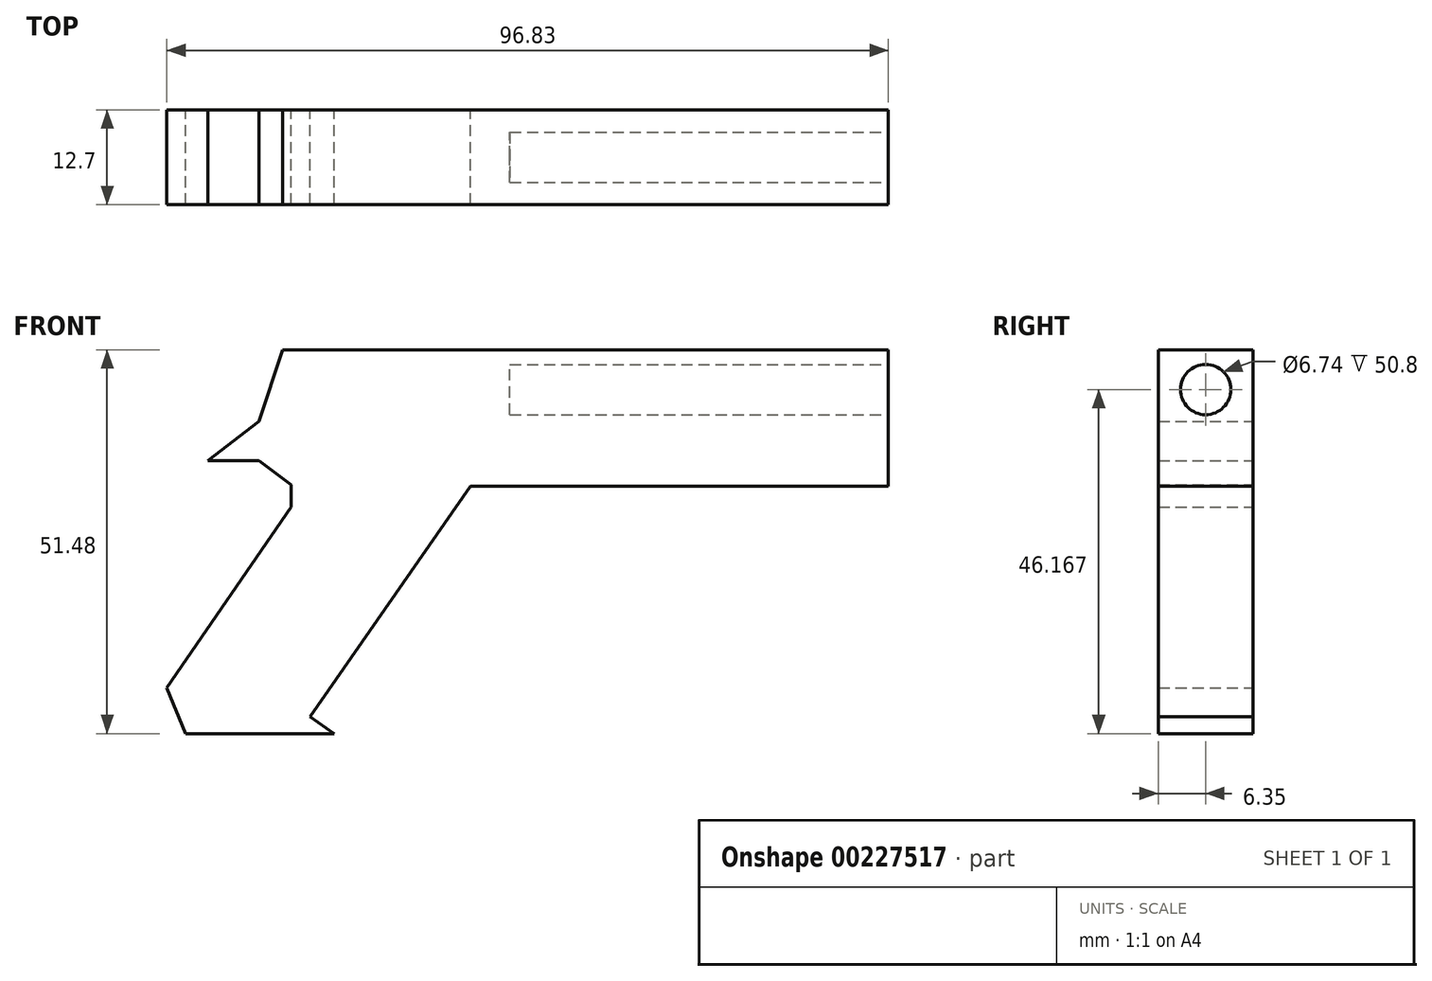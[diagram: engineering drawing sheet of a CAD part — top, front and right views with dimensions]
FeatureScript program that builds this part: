
annotation { "Feature Type Name" : "Feature", "Feature Type Description" : "" }
export const myFeature = defineFeature(function(context is Context, id is Id, definition is map)
    precondition{}
    {
        {
            var Q0;
            Q0=qCreatedBy(makeId("Front.planeOp"),FACE);
            var sketch = newSketch(context, id + "F0", { "sketchPlane" : qUnion([Q0])});
            skLineSegment(sketch, "E0", {"start": v(-32.16, 42.92) * mm, "end": v(49.1, 42.92) * mm});
            skLineSegment(sketch, "E1", {"start": v(49.1, 42.92) * mm, "end": v(49.1, 24.6) * mm});
            skLineSegment(sketch, "E2", {"start": v(49.1, 24.6) * mm, "end": v(-6.98, 24.6) * mm});
            skLineSegment(sketch, "E3", {"start": v(-6.98, 24.6) * mm, "end": v(-28.5, -6.3) * mm});
            skLineSegment(sketch, "E4", {"start": v(-28.5, -6.3) * mm, "end": v(-25.26, -8.56) * mm});
            skLineSegment(sketch, "E5", {"start": v(-25.26, -8.56) * mm, "end": v(-45.21, -8.56) * mm});
            skLineSegment(sketch, "E6", {"start": v(-45.21, -8.56) * mm, "end": v(-47.73, -2.4) * mm});
            skLineSegment(sketch, "E7", {"start": v(-47.73, -2.4) * mm, "end": v(-31.02, 21.86) * mm});
            skLineSegment(sketch, "E8", {"start": v(-31.02, 21.86) * mm, "end": v(-31.02, 24.84) * mm});
            skLineSegment(sketch, "E9", {"start": v(-31.02, 24.84) * mm, "end": v(-35.37, 28.04) * mm});
            skLineSegment(sketch, "E10", {"start": v(-35.37, 28.04) * mm, "end": v(-42.24, 28.04) * mm});
            skLineSegment(sketch, "E11", {"start": v(-42.24, 28.04) * mm, "end": v(-35.37, 33.3) * mm});
            skLineSegment(sketch, "E12", {"start": v(-35.37, 33.3) * mm, "end": v(-32.16, 42.92) * mm});
            skSolve(sketch);
        }
        {
            var Q0;
            Q0 = qSketchRegion(id + "F0", true);
            extrude(context, id + "F1", {"entities" : qUnion([Q0]), "endBound" : BoundingType.SYMMETRIC, "depth" : 12.7 * mm});
        }
        {
            var Q0;
            Q0=makeQuery(id+"F1.opExtrude","SWEPT_FACE",FACE,{"disambiguationData":[OSD([sQuery(id+"F0.wireOp",EDGE,"E1")])]});
            var sketch = newSketch(context, id + "F2", { "sketchPlane" : qUnion([Q0])});
            skCircle(sketch, "E13", {"center": v(0, 37.6) * mm, "radius": 3.37 * mm});
            skSolve(sketch);
        }
        {
            var Q0;
            Q0 = qSketchRegion(id + "F2", true);
            extrude(context, id + "F3", {"entities" : qUnion([Q0]), "operationType" : NewBodyOperationType.REMOVE, "oppositeDirection" : true, "depth" : 50.8 * mm});
        }
    });
